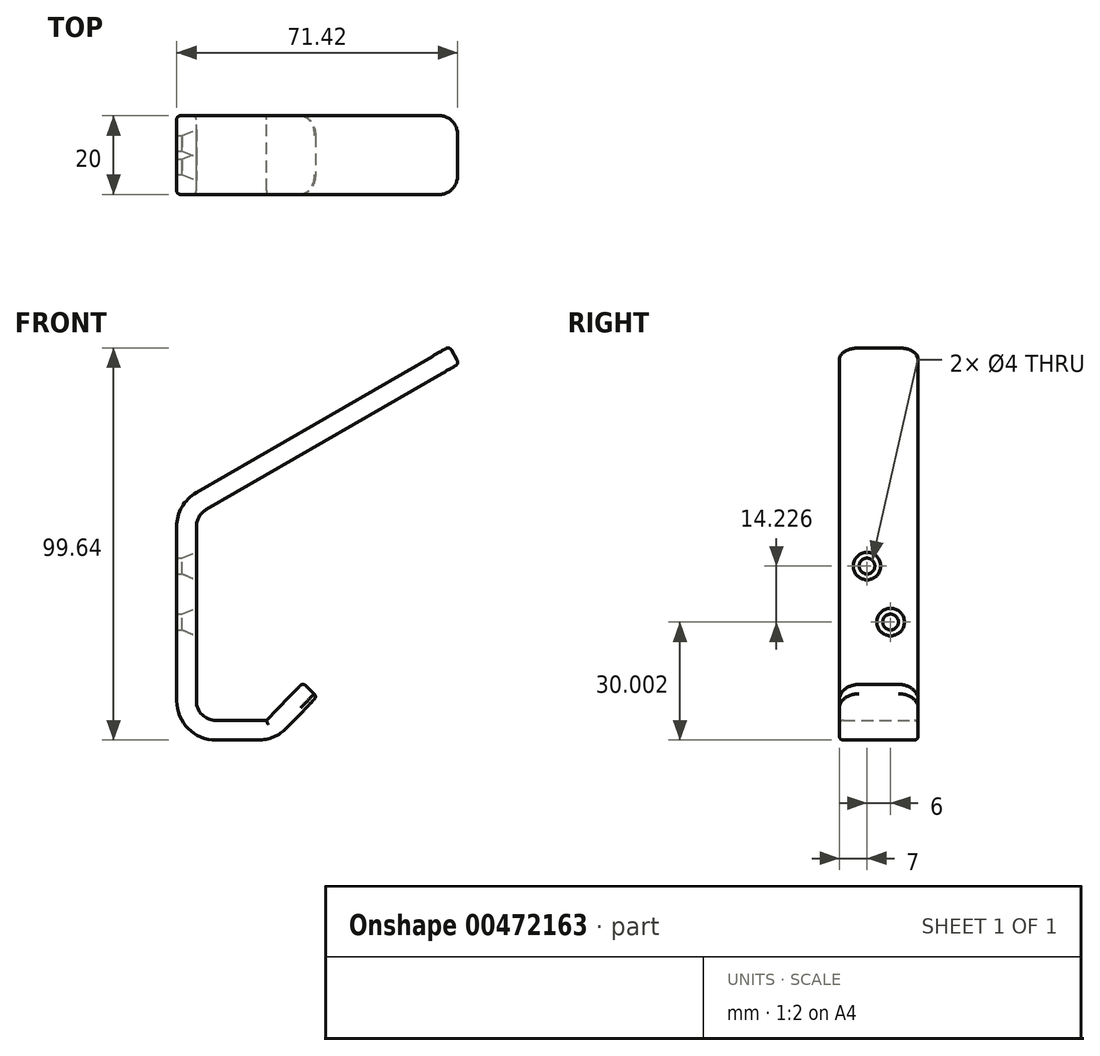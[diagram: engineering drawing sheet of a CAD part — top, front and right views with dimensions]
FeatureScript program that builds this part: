
annotation { "Feature Type Name" : "Feature", "Feature Type Description" : "" }
export const myFeature = defineFeature(function(context is Context, id is Id, definition is map)
    precondition{}
    {
        {
            var Q0;
            Q0=qCreatedBy(makeId("Front.planeOp"),FACE);
            var sketch = newSketch(context, id + "F0", { "sketchPlane" : qUnion([Q0])});
            skLineSegment(sketch, "E0", {"start": v(13.08, -14.25) * mm, "end": v(-11.92, -14.25) * mm});
            skLineSegment(sketch, "E1", {"start": v(-11.92, -14.25) * mm, "end": v(-11.92, 45.75) * mm});
            skLineSegment(sketch, "E2", {"start": v(-11.92, 45.75) * mm, "end": v(57.36, 85.75) * mm});
            skLineSegment(sketch, "E3", {"start": v(57.36, 85.75) * mm, "end": v(59.86, 81.42) * mm});
            skLineSegment(sketch, "E4", {"start": v(59.86, 81.42) * mm, "end": v(-6.92, 42.87) * mm});
            skPoint(sketch, "E5.end.orphan", {"position": v(23.74, -3.18) * mm});
            skLineSegment(sketch, "E6", {"start": v(13.08, -14.25) * mm, "end": v(23.74, -3.18) * mm});
            skPoint(sketch, "E7.end.orphan", {"position": v(20.15, 0.3) * mm});
            skLineSegment(sketch, "E8", {"start": v(20.15, 0.3) * mm, "end": v(23.74, -3.18) * mm});
            skLineSegment(sketch, "E9", {"start": v(20.15, 0.3) * mm, "end": v(10.87, -9.25) * mm});
            skLineSegment(sketch, "E10", {"start": v(10.87, -9.25) * mm, "end": v(-6.92, -9.25) * mm});
            skLineSegment(sketch, "E11", {"start": v(-6.92, -9.25) * mm, "end": v(-6.92, 42.87) * mm});
            skSolve(sketch);
        }
        {
            var Q0;
            Q0 = qSketchRegion(id + "F0", true);
            extrude(context, id + "F1", {"entities" : qUnion([Q0]), "depth" : 20 * mm});
        }
        {
            var Q0;
            Q0=makeQuery(id+"F1.opExtrude","SWEPT_EDGE",EDGE,{"disambiguationData":[OSD([sQuery(id+"F0.wireOp",EDGE,"E0"),sQuery(id+"F0.wireOp",EDGE,"E1")])]});
            fillet(context, id + "F2", {"entities" : qUnion([Q0]), "radius" : 10 * mm, "tangentPropagation" : true, "allowEdgeOverflow" : false});
        }
        {
            var Q0;
            Q0=makeQuery(id+"F1.opExtrude","SWEPT_EDGE",EDGE,{"disambiguationData":[OSD([sQuery(id+"F0.wireOp",EDGE,"cWVkua7E-6hmU-I1Vy-KUL2-vaDqfP17Zomh"),sQuery(id+"F0.wireOp",EDGE,"E0")])]});
            fillet(context, id + "F3", {"entities" : qUnion([Q0]), "radius" : 10 * mm, "tangentPropagation" : true, "allowEdgeOverflow" : false});
        }
        {
            var Q0;
            Q0=makeQuery(id+"F1.opExtrude","SWEPT_EDGE",EDGE,{"disambiguationData":[OSD([sQuery(id+"F0.wireOp",EDGE,"E1"),sQuery(id+"F0.wireOp",EDGE,"E2")])]});
            fillet(context, id + "F4", {"entities" : qUnion([Q0]), "radius" : 10 * mm, "tangentPropagation" : true, "allowEdgeOverflow" : false});
        }
        {
            var Q0;
            Q0=makeQuery(id+"F1.opExtrude","SWEPT_EDGE",EDGE,{"disambiguationData":[OSD([sQuery(id+"F0.wireOp",EDGE,"E10"),sQuery(id+"F0.wireOp",EDGE,"E11")])]});
            fillet(context, id + "F5", {"entities" : qUnion([Q0]), "radius" : 5 * mm, "tangentPropagation" : true, "allowEdgeOverflow" : false});
        }
        {
            var Q0;
            Q0=makeQuery(id+"F1.opExtrude","SWEPT_EDGE",EDGE,{"disambiguationData":[OSD([sQuery(id+"F0.wireOp",EDGE,"E4"),sQuery(id+"F0.wireOp",EDGE,"E11")])]});
            fillet(context, id + "F6", {"entities" : qUnion([Q0]), "radius" : 5 * mm, "tangentPropagation" : true, "allowEdgeOverflow" : false});
        }
        {
            var Q0;
            Q0=makeQuery(id+"F1.opExtrude","CAP_EDGE",EDGE,{"disambiguationData":[OSD([sQuery(id+"F0.wireOp",EDGE,"E8")])],"isStart":false});
            fillet(context, id + "F7", {"entities" : qUnion([Q0]), "radius" : 5 * mm, "tangentPropagation" : true, "allowEdgeOverflow" : false});
        }
        {
            var Q0;
            Q0=makeQuery(id+"F1.opExtrude","CAP_EDGE",EDGE,{"disambiguationData":[OSD([sQuery(id+"F0.wireOp",EDGE,"E8")])],"isStart":true});
            fillet(context, id + "F8", {"entities" : qUnion([Q0]), "radius" : 5 * mm, "tangentPropagation" : true, "allowEdgeOverflow" : false});
        }
        {
            var Q0;
            Q0=makeQuery(id+"F1.opExtrude","CAP_EDGE",EDGE,{"disambiguationData":[OSD([sQuery(id+"F0.wireOp",EDGE,"E3")])],"isStart":false});
            fillet(context, id + "F9", {"entities" : qUnion([Q0]), "radius" : 5 * mm, "tangentPropagation" : true, "allowEdgeOverflow" : false});
        }
        {
            var Q0;
            Q0=makeQuery(id+"F1.opExtrude","CAP_EDGE",EDGE,{"disambiguationData":[OSD([sQuery(id+"F0.wireOp",EDGE,"E3")])],"isStart":true});
            fillet(context, id + "F10", {"entities" : qUnion([Q0]), "radius" : 5 * mm, "tangentPropagation" : true, "allowEdgeOverflow" : false});
        }
        {
            var Q0;
            Q0=makeQuery(id+"F1.opExtrude","CAP_EDGE",EDGE,{"disambiguationData":[OSD([sQuery(id+"F0.wireOp",EDGE,"E4")])],"isStart":false});
            fillet(context, id + "F11", {"entities" : qUnion([Q0]), "radius" : 1 * mm, "tangentPropagation" : true, "allowEdgeOverflow" : false});
        }
        {
            var Q0;
            Q0=makeQuery(id+"F1.opExtrude","CAP_EDGE",EDGE,{"disambiguationData":[OSD([sQuery(id+"F0.wireOp",EDGE,"E6")])],"isStart":false});
            fillet(context, id + "F12", {"entities" : qUnion([Q0]), "radius" : 1 * mm, "tangentPropagation" : true, "allowEdgeOverflow" : false});
        }
        {
            var Q0;
            Q0=makeQuery(id+"F1.opExtrude","CAP_EDGE",EDGE,{"disambiguationData":[OSD([sQuery(id+"F0.wireOp",EDGE,"E9")])],"isStart":false});
            fillet(context, id + "F13", {"entities" : qUnion([Q0]), "radius" : 1 * mm, "tangentPropagation" : true, "allowEdgeOverflow" : false});
        }
        {
            var Q0;
            Q0=makeQuery(id+"F1.opExtrude","SWEPT_FACE",FACE,{"disambiguationData":[OSD([sQuery(id+"F0.wireOp",EDGE,"E11")])]});
            var sketch = newSketch(context, id + "F14", { "sketchPlane" : qUnion([Q0])});
            skPoint(sketch, "E12", {"position": v(-13, 29.98) * mm});
            skPoint(sketch, "E13", {"position": v(-7, 15.75) * mm});
            skSolve(sketch);
        }
        {
            var Q0;
            Q0=sQuery(id+"F14.wireOp",VERTEX,"E12");
            var Q1;
            Q1=makeQuery(id+"F1.opExtrude","SWEPT_BODY",BODY,{"disambiguationData":[OSD([sQuery(id+"F0.wireOp",EDGE,"E0"),sQuery(id+"F0.wireOp",EDGE,"E1"),sQuery(id+"F0.wireOp",EDGE,"E2"),sQuery(id+"F0.wireOp",EDGE,"E3"),sQuery(id+"F0.wireOp",EDGE,"E4"),sQuery(id+"F0.wireOp",EDGE,"E6"),sQuery(id+"F0.wireOp",EDGE,"E8"),sQuery(id+"F0.wireOp",EDGE,"E9"),sQuery(id+"F0.wireOp",EDGE,"E10"),sQuery(id+"F0.wireOp",EDGE,"E11")])]});
            hole(context, id + "F15", {"style" : HoleStyle.C_SINK, "endStyle" : HoleEndStyle.THROUGH, "holeDiameter" : 4 * mm, "cSinkDiameter" : 7 * mm, "cSinkAngle" : 45 * degree, "isTappedThrough" : true, "tappedDepth" : 12 * mm, "tapClearance" : 3, "locations" : qUnion([Q0]), "scope" : qUnion([Q1])});
        }
        {
            var Q0;
            Q0=makeQuery(id+"F1.opExtrude","SWEPT_FACE",FACE,{"disambiguationData":[OSD([sQuery(id+"F0.wireOp",EDGE,"E11")])]});
            var sketch = newSketch(context, id + "F16", { "sketchPlane" : qUnion([Q0])});
            skPoint(sketch, "E14", {"position": v(-7, 15.75) * mm});
            skSolve(sketch);
        }
        {
            var Q0;
            Q0=sQuery(id+"F16.wireOp",VERTEX,"E14");
            var Q1;
            Q1=makeQuery(id+"F1.opExtrude","SWEPT_BODY",BODY,{"disambiguationData":[OSD([sQuery(id+"F0.wireOp",EDGE,"E0"),sQuery(id+"F0.wireOp",EDGE,"E1"),sQuery(id+"F0.wireOp",EDGE,"E2"),sQuery(id+"F0.wireOp",EDGE,"E3"),sQuery(id+"F0.wireOp",EDGE,"E4"),sQuery(id+"F0.wireOp",EDGE,"E6"),sQuery(id+"F0.wireOp",EDGE,"E8"),sQuery(id+"F0.wireOp",EDGE,"E9"),sQuery(id+"F0.wireOp",EDGE,"E10"),sQuery(id+"F0.wireOp",EDGE,"E11")])]});
            hole(context, id + "F17", {"style" : HoleStyle.C_SINK, "endStyle" : HoleEndStyle.THROUGH, "holeDiameter" : 4 * mm, "cSinkDiameter" : 7 * mm, "cSinkAngle" : 45 * degree, "isTappedThrough" : true, "tappedDepth" : 12 * mm, "tapClearance" : 3, "locations" : qUnion([Q0]), "scope" : qUnion([Q1])});
        }
    });
